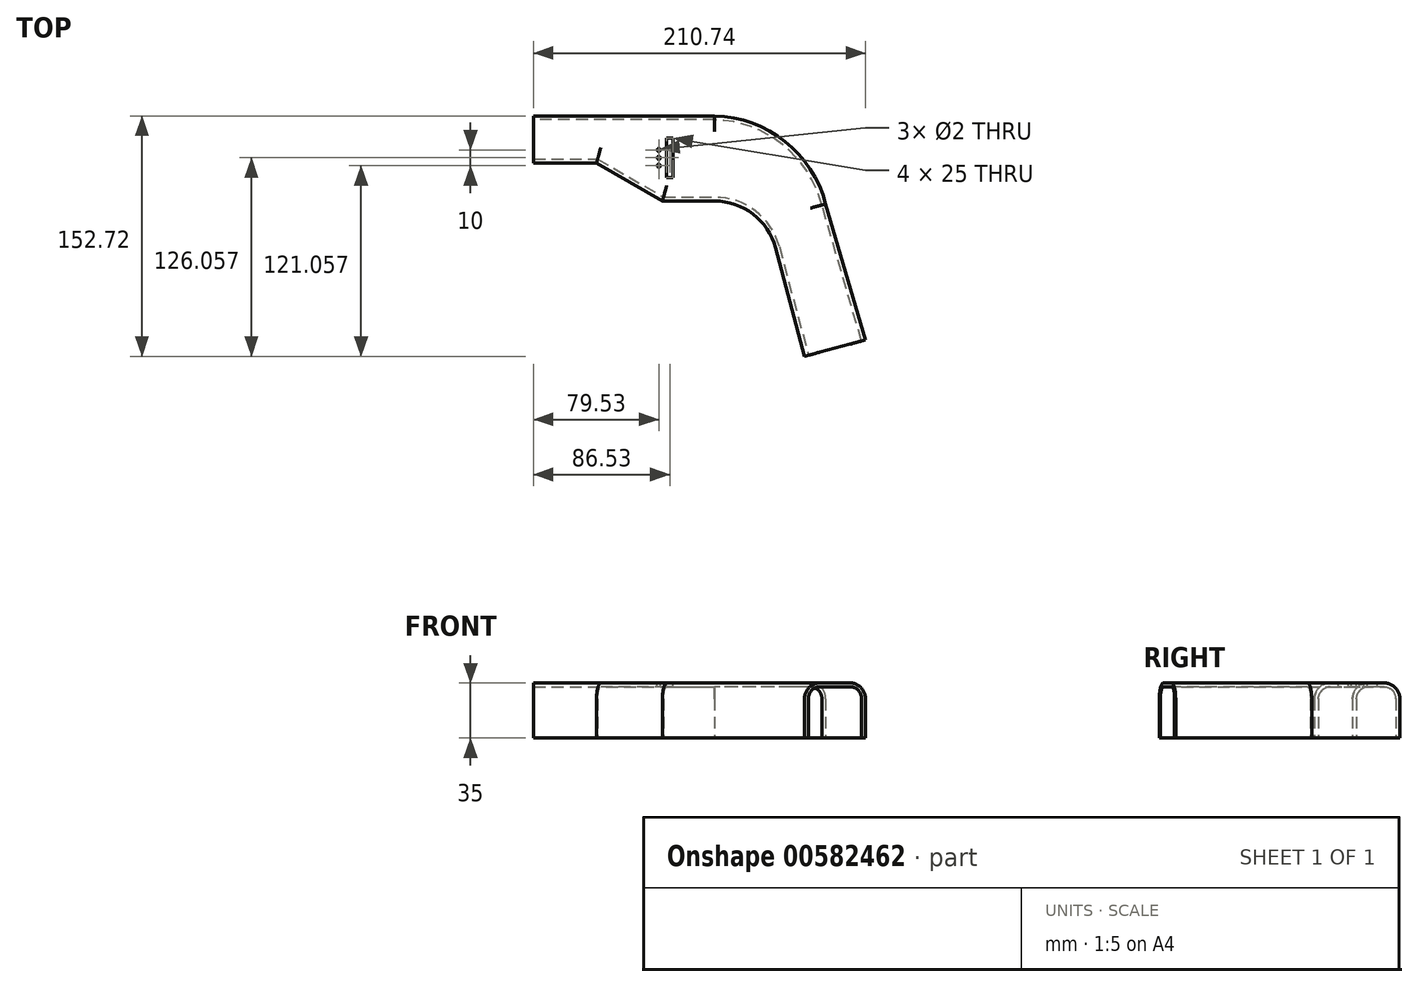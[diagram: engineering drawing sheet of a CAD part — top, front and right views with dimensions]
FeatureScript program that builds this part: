
annotation { "Feature Type Name" : "Feature", "Feature Type Description" : "" }
export const myFeature = defineFeature(function(context is Context, id is Id, definition is map)
    precondition{}
    {
        {
            var Q0;
            Q0=qCreatedBy(makeId("Top.planeOp"),FACE);
            var sketch = newSketch(context, id + "F0", { "sketchPlane" : qUnion([Q0])});
            skLineSegment(sketch, "E0", {"start": v(0, 0) * mm, "end": v(-115, 0) * mm});
            skLineSegment(sketch, "E1", {"start": v(-115, 0) * mm, "end": v(-115, -30) * mm});
            skLineSegment(sketch, "E2", {"start": v(-115, -30) * mm, "end": v(-75, -30) * mm});
            skPoint(sketch, "E3.end.orphan", {"position": v(0, -54.16) * mm});
            skLineSegment(sketch, "E4", {"start": v(-75, -30) * mm, "end": v(-33.15, -54.16) * mm});
            skLineSegment(sketch, "E5", {"start": v(-33.15, -54.16) * mm, "end": v(0, -54.16) * mm});
            skArc(sketch, "E6", {"start": v(38.64, -83.8) * mm, "mid": v(24.35, -62.43) * mm, "end": v(0, -54.16) * mm});
            skArc(sketch, "E7", {"start": v(70.52, -55.97) * mm, "mid": v(44.6, -16.23) * mm, "end": v(0, 0) * mm});
            skPoint(sketch, "E8", {"position": v(0, -149.94) * mm});
            skPoint(sketch, "E9", {"position": v(0, -134.16) * mm});
            skLineSegment(sketch, "E10", {"start": v(38.64, -83.8) * mm, "end": v(57.1, -152.72) * mm});
            skLineSegment(sketch, "E11", {"start": v(57.1, -152.72) * mm, "end": v(95.74, -142.37) * mm});
            skLineSegment(sketch, "E12", {"start": v(95.74, -142.37) * mm, "end": v(70.52, -55.97) * mm});
            skSolve(sketch);
        }
        {
            var Q0;
            Q0 = qSketchRegion(id + "F0", true);
            extrude(context, id + "F1", {"entities" : qUnion([Q0]), "depth" : 35 * mm, "offsetDistance" : 25 * mm});
        }
        {
            var Q0;
            Q0=makeQuery(id+"F1.opExtrude","CAP_EDGE",EDGE,{"disambiguationData":[OSD([sQuery(id+"F0.wireOp",EDGE,"E2")])],"isStart":false});
            var Q1;
            Q1=makeQuery(id+"F1.opExtrude","CAP_EDGE",EDGE,{"disambiguationData":[OSD([sQuery(id+"F0.wireOp",EDGE,"E0")])],"isStart":false});
            var Q2;
            Q2=makeQuery(id+"F1.opExtrude","CAP_EDGE",EDGE,{"disambiguationData":[OSD([sQuery(id+"F0.wireOp",EDGE,"E4")])],"isStart":false});
            var Q3;
            Q3=makeQuery(id+"F1.opExtrude","CAP_EDGE",EDGE,{"disambiguationData":[OSD([sQuery(id+"F0.wireOp",EDGE,"E5")])],"isStart":false});
            var Q4;
            Q4=makeQuery(id+"F1.opExtrude","CAP_EDGE",EDGE,{"disambiguationData":[OSD([sQuery(id+"F0.wireOp",EDGE,"E6")])],"isStart":false});
            var Q5;
            Q5=makeQuery(id+"F1.opExtrude","CAP_EDGE",EDGE,{"disambiguationData":[OSD([sQuery(id+"F0.wireOp",EDGE,"E12")])],"isStart":false});
            var Q6;
            Q6=makeQuery(id+"F1.opExtrude","CAP_EDGE",EDGE,{"disambiguationData":[OSD([sQuery(id+"F0.wireOp",EDGE,"E7")])],"isStart":false});
            fillet(context, id + "F2", {"entities" : qUnion([Q0, Q1, Q2, Q3, Q4, Q5, Q6]), "radius" : 10 * mm, "tangentPropagation" : true, "allowEdgeOverflow" : false});
        }
        {
            var Q0;
            Q0=makeQuery(id+"F1.opExtrude","SWEPT_FACE",FACE,{"disambiguationData":[OSD([sQuery(id+"F0.wireOp",EDGE,"E11")])]});
            var Q1;
            Q1=makeQuery(id+"F1.opExtrude","CAP_FACE",FACE,{"disambiguationData":[OSD([sQuery(id+"F0.wireOp",EDGE,"E0"),sQuery(id+"F0.wireOp",EDGE,"E1"),sQuery(id+"F0.wireOp",EDGE,"E2"),sQuery(id+"F0.wireOp",EDGE,"E4"),sQuery(id+"F0.wireOp",EDGE,"E5"),sQuery(id+"F0.wireOp",EDGE,"E6"),sQuery(id+"F0.wireOp",EDGE,"E7"),sQuery(id+"F0.wireOp",EDGE,"E10"),sQuery(id+"F0.wireOp",EDGE,"E11"),sQuery(id+"F0.wireOp",EDGE,"E12")])],"isStart":true});
            var Q2;
            Q2=makeQuery(id+"F1.opExtrude","SWEPT_FACE",FACE,{"disambiguationData":[OSD([sQuery(id+"F0.wireOp",EDGE,"E1")])]});
            shell(context, id + "F3", {"entities" : qUnion([Q0, Q1, Q2]), "thickness" : 2.5 * mm});
        }
        {
            var Q0;
            Q0=makeQuery(id+"F1.opExtrude","CAP_FACE",FACE,{"disambiguationData":[OSD([sQuery(id+"F0.wireOp",EDGE,"E0"),sQuery(id+"F0.wireOp",EDGE,"E1"),sQuery(id+"F0.wireOp",EDGE,"E2"),sQuery(id+"F0.wireOp",EDGE,"E4"),sQuery(id+"F0.wireOp",EDGE,"E5"),sQuery(id+"F0.wireOp",EDGE,"E6"),sQuery(id+"F0.wireOp",EDGE,"E7"),sQuery(id+"F0.wireOp",EDGE,"E10"),sQuery(id+"F0.wireOp",EDGE,"E11"),sQuery(id+"F0.wireOp",EDGE,"E12")])],"isStart":false});
            var sketch = newSketch(context, id + "F4", { "sketchPlane" : qUnion([Q0])});
            skLineSegment(sketch, "E13", {"start": v(-30.47, -39.16) * mm, "end": v(-26.47, -39.16) * mm});
            skLineSegment(sketch, "E14", {"start": v(-26.47, -39.16) * mm, "end": v(-26.47, -14.16) * mm});
            skLineSegment(sketch, "E15", {"start": v(-26.47, -14.16) * mm, "end": v(-30.47, -14.16) * mm});
            skLineSegment(sketch, "E16", {"start": v(-30.47, -14.16) * mm, "end": v(-30.47, -39.16) * mm});
            skCircle(sketch, "E17", {"center": v(-35.47, -26.66) * mm, "radius": 1 * mm});
            skCircle(sketch, "E18", {"center": v(-35.47, -31.66) * mm, "radius": 1 * mm});
            skCircle(sketch, "E19", {"center": v(-35.47, -21.66) * mm, "radius": 1 * mm});
            skPoint(sketch, "E20.start.orphan", {"position": v(-30.47, -44.16) * mm});
            skSolve(sketch);
        }
        {
            var Q0;
            Q0 = qSketchRegion(id + "F4", true);
            extrude(context, id + "F5", {"entities" : qUnion([Q0]), "operationType" : NewBodyOperationType.REMOVE, "oppositeDirection" : true, "depth" : 25 * mm, "offsetDistance" : 25 * mm});
        }
    });
